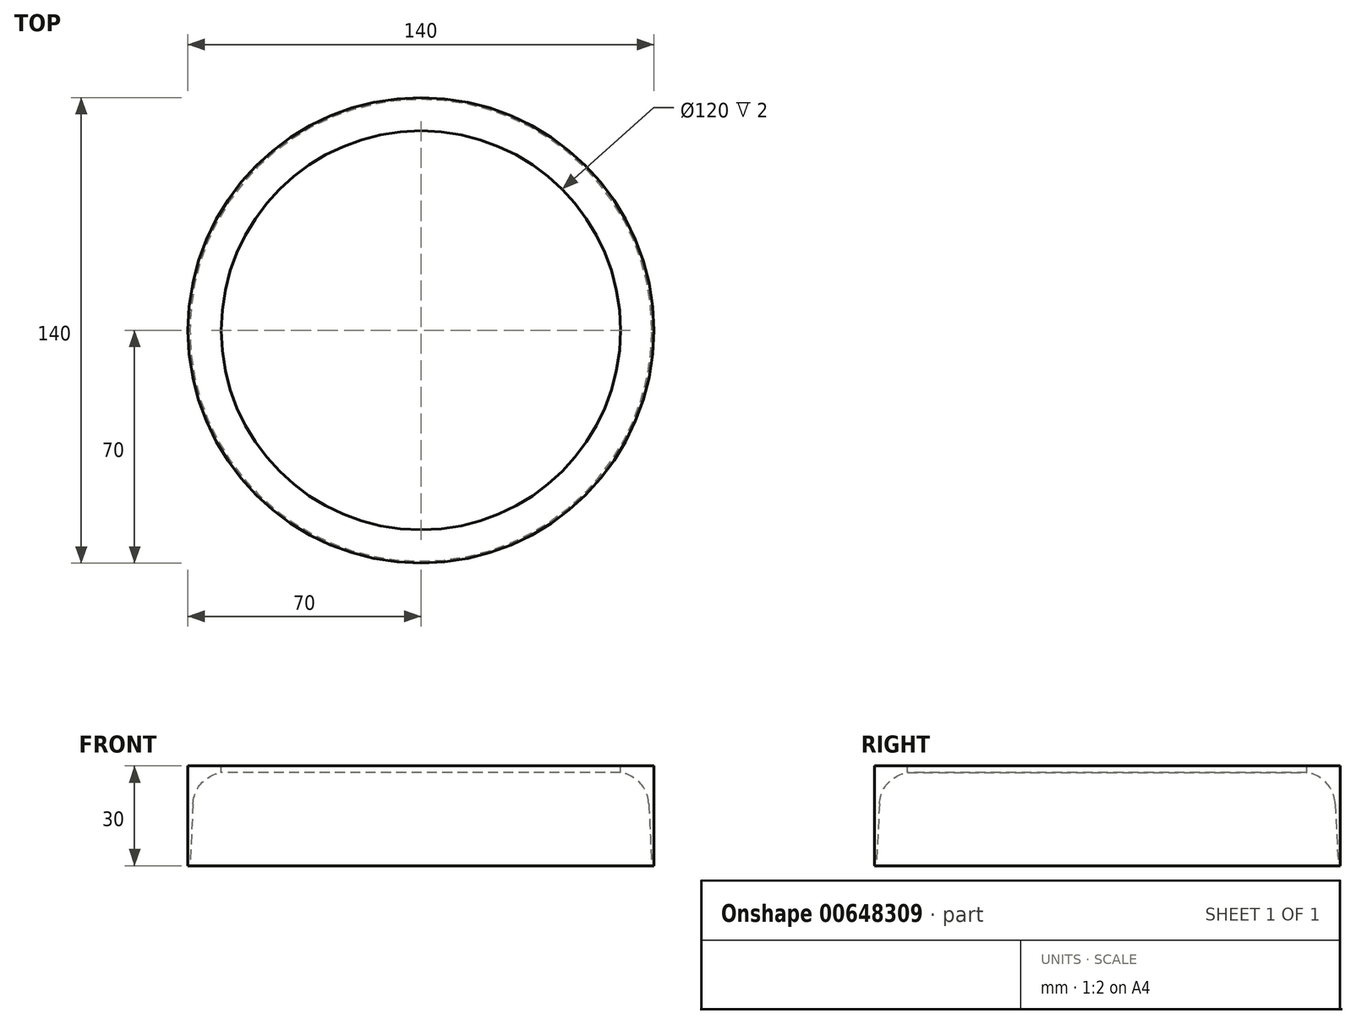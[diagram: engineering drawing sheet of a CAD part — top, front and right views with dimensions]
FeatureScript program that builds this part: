
annotation { "Feature Type Name" : "Feature", "Feature Type Description" : "" }
export const myFeature = defineFeature(function(context is Context, id is Id, definition is map)
    precondition{}
    {
        {
            var Q0;
            Q0=qCreatedBy(makeId("Front.planeOp"),FACE);
            var sketch = newSketch(context, id + "F0", { "sketchPlane" : qUnion([Q0])});
            skLineSegment(sketch, "E0.left", {"start": v(77.5, -15) * mm, "end": v(77.5, 15) * mm, "construction": true});
            skPoint(sketch, "E0.middle", {"position": v(0, 0) * mm});
            skLineSegment(sketch, "E1", {"start": v(-60, 15) * mm, "end": v(-70, 15) * mm});
            skLineSegment(sketch, "E2", {"start": v(-70, -15) * mm, "end": v(-70, 15) * mm});
            skLineSegment(sketch, "E3", {"start": v(-70, -15) * mm, "end": v(-69.4, -15) * mm});
            skLineSegment(sketch, "E4", {"start": v(-69.4, -15) * mm, "end": v(-68.47, 3.65) * mm});
            skLineSegment(sketch, "E5.bottom", {"start": v(-70, 15) * mm, "end": v(-60, 15) * mm});
            skLineSegment(sketch, "E5.left", {"start": v(-70, 15) * mm, "end": v(-70, 13) * mm});
            skLineSegment(sketch, "E5.right", {"start": v(-60, 15) * mm, "end": v(-60, 13) * mm});
            skArc(sketch, "E6", {"start": v(-60, 13) * mm, "mid": v(-65.9, 9.83) * mm, "end": v(-68.47, 3.65) * mm});
            skLineSegment(sketch, "E7", {"start": v(0, 43.98) * mm, "end": v(0, -47.4) * mm, "construction": true});
            skSolve(sketch);
        }
        {
            var Q0;
            Q0 = qSketchRegion(id + "F0", true);
            var Q1;
            Q1=sQuery(id+"F0.wireOp",EDGE,"E7");
            revolve(context, id + "F1", {"entities" : qUnion([Q0]), "axis" : qUnion([Q1]), "revolveType" : RevolveType.FULL});
        }
    });
